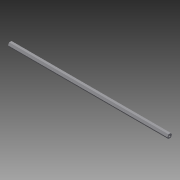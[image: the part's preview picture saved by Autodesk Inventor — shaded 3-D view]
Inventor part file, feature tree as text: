
AUTODESK INVENTOR PART (.ipt)
format: ipt  version: 2015 SP1 (Build 190203100, 203)  size: 105,472 bytes
history: native  units: in
note: dims shown in document units (in); Inventor stores cm internally (conversion verified against a paired STEP export)
features: extrude x2, sketch x2, thread x1
ambient origin geometry x8: Origin, YZ Plane, XZ Plane, XY Plane, X Axis, Y Axis, Z Axis, Center Point
bodies: Solid1 (feature_tree)
feature tree (5):
  extrude  "Extrusion1"  Depth=0.5in
  extrude  "Extrusion2"  Depth=0.5in
  thread  "Thread1"  [1 undecoded]
  sketch  "Sketch1"  dims[d0=0.5in d1=0.5in]
  sketch  "Sketch2"  dims[d2=0.5in d3=0.25in d4=120.0deg d5=120.0deg d6=0.25in d7=0.25in d8=19.625in d9=0.0in d10=0.25in d11=0.5in d12=0.0in d13=1.0in d14=0.0in]
note: 1 required parameter value undecoded (feature->parameter linkage not recoverable at this tier; creation-order binding heuristic only, values carry confidence <= 0.55)
